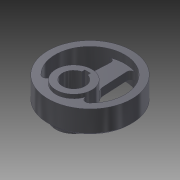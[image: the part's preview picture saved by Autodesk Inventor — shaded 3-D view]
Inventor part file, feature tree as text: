
AUTODESK INVENTOR PART (.ipt)
format: ipt  version: 2011 SP2 (Build 150309200, 309)  size: 160,768 bytes
history: native  units: mm
features: sketch x3, extrude x3, projected_geometry x2, plane x1, chamfer x1
ambient origin geometry x8: Origin, YZ Plane, XZ Plane, XY Plane, X Axis, Y Axis, Z Axis, Center Point
bodies: Solid1 (feature_tree)
feature tree (10):
  sketch  "Sketch1"  dims[d0=70.0mm d1=58.0mm]
  extrude  "Extrusion1"  Depth=58.0mm
  plane  "Work Plane1"
  sketch  "Sketch2"  dims[d2=19.0mm d3=30.0mm]
  extrude  "Extrusion2"  Depth=30.0mm
  sketch  "Sketch3"  dims[d4=27.0mm d5=42.2mm d6=9.5mm d7=38.0mm d8=65.0mm d13=7.0mm d14=7.0mm d15=3.8mm d16=17.0mm d17=6.0mm d18=0.523599mm d19=6.0mm d20=17.0mm d21=0.523599mm d22=57.15mm d23=0.0mm d24=3.0mm d25=19.45mm d26=24.7mm d27=3.875mm d28=9.125mm d29=9.125mm d30=3.875mm d31=0.0mm d32=0.0mm d33=6.45mm d34=12.5mm d35=22.125mm d36=16.075mm d37=22.125mm d38=16.075mm d39=0.0mm d40=0.0mm d41=3.0mm d42=2.0mm d43=45.0deg]
  extrude  "Extrusion3"  Depth=42.2mm
  chamfer  "Chamfer1"  Distance=9.5mm
  projected_geometry  "Projected Loop1"
  projected_geometry  "Projected Loop2"
